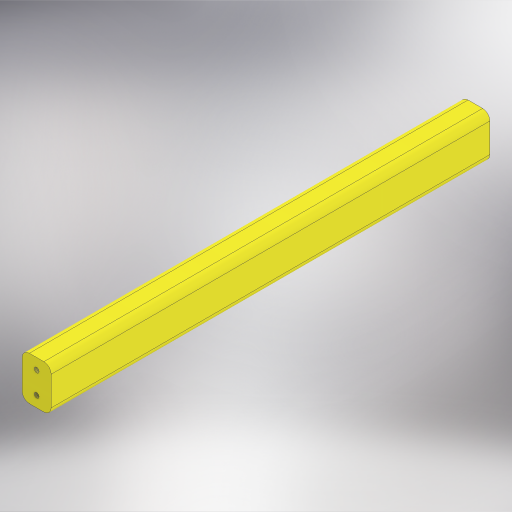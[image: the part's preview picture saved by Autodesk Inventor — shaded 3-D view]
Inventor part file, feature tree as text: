
AUTODESK INVENTOR PART (.ipt)
format: ipt  version: 2024 (Build 280153000, 153)  size: 331,776 bytes
history: native  units: in
note: dims shown in document units (in); Inventor stores cm internally (conversion verified against a paired STEP export)
features: sketch x2, hole x2, extrude x1, fillet x1
ambient origin geometry x8: Origin, YZ Plane, XZ Plane, XY Plane, X Axis, Y Axis, Z Axis, Center Point
bodies: Solid1 (feature_tree)
feature tree (6):
  extrude  "Extrusion1"  Depth=0.75in
  sketch  "Sketch2"  dims[d0=0.5in d1=0.75in d2=7.54in d3=0.0in]
  sketch  "Sketch3"  dims[d4=0.112in d5=0.112in d18=0.125in d19=0.0849in d20=0.75in d21=0.375in d22=0.25in d23=0.5635in d24=1.0in d25=0.8108in d26=0.0849in d27=0.75in d28=0.375in d29=0.25in d30=0.5635in d31=1.0in d32=0.8108in]
  fillet  "Fillet1"  Radius=7.54in
  hole  "Hole1"  [1 undecoded]
  hole  "Hole2"  [1 undecoded]
note: 2 required parameter values undecoded (feature->parameter linkage not recoverable at this tier; creation-order binding heuristic only, values carry confidence <= 0.55)
